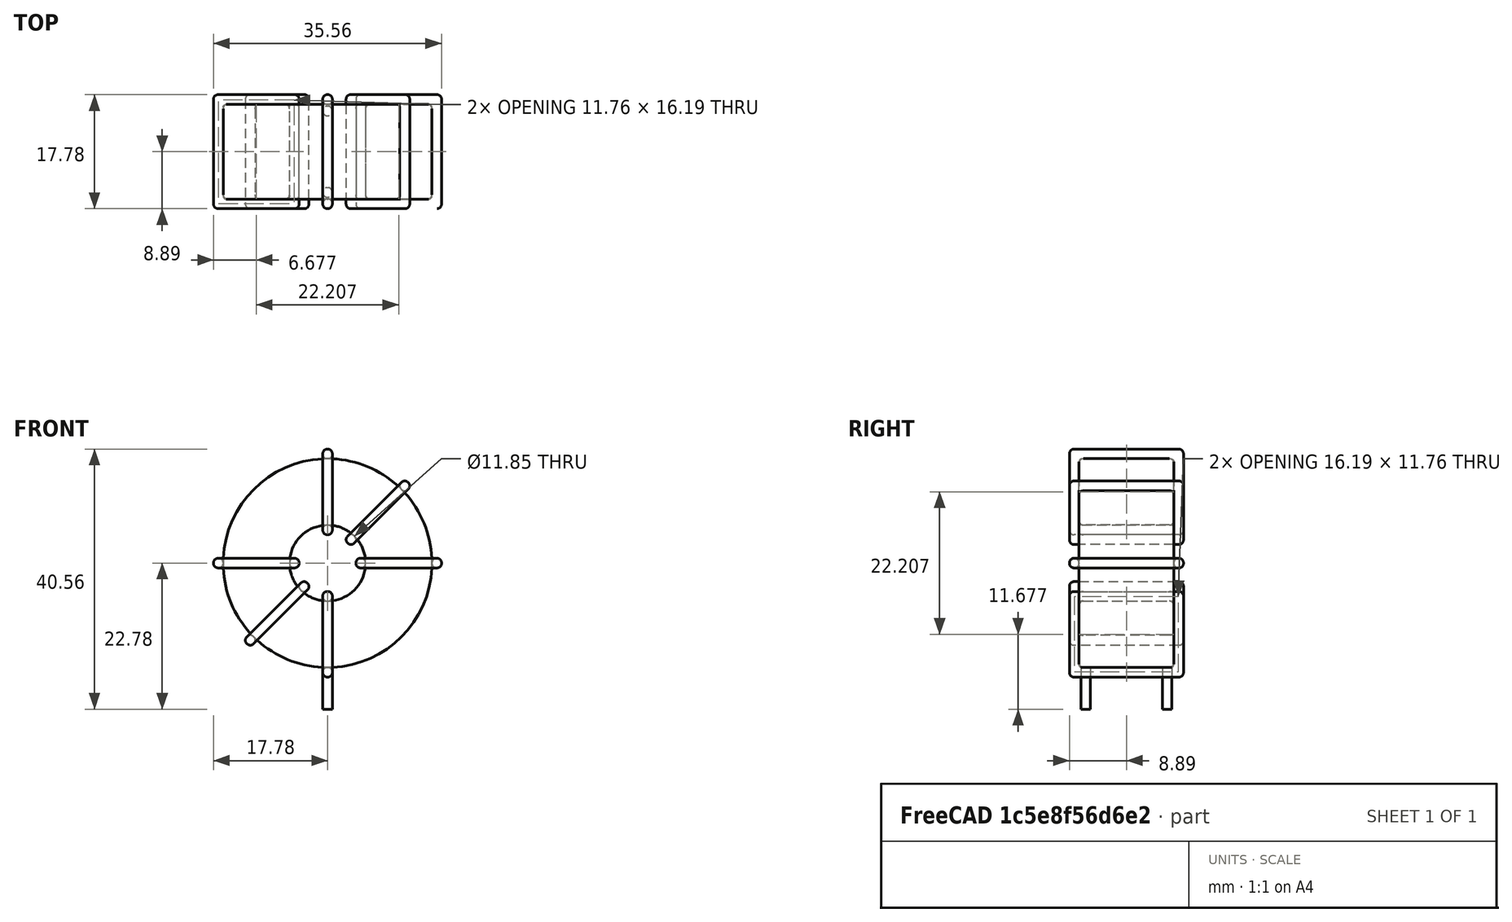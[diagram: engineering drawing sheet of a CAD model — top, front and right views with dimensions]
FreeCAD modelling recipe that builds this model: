
FCSTD DOCUMENT  (FreeCAD 0.16R6703 (Git))
Label: L_Toroid_Vertical_L35.6mm_W17.8mm_P12.70mm_Pulse_E
License: All rights reserved
LicenseURL: http://en.wikipedia.org/wiki/All_rights_reserved
objects: Sketcher::SketchObject×6, PartDesign::Pad×6, PartDesign::Fillet×5, Spreadsheet::Sheet×1
note: 23 computed .brp shape members not serialized (recipe doc carries the construction recipe); baked Part::Feature solids carry a one-line shape summary decoded from their .brp

FEATURE [Spreadsheet::Sheet] Spreadsheet  label="dimensions"
  cells = A1=Wx; B1(Wx)=35.56; C1(WW)=11.85333333333333; D1=35.56; A2=Wy; B2(Wy)=17.78; D2=17.78; A3=RM; B3(RMx)=12.7; C3(RMy)=0; A4=d_wire; B4(d_wire)=1.5; A5=H; B5(H)=35.56; A6=offsetx; B6(offsetx)=17.78
FEATURE [Sketcher::SketchObject] Sketch
  Placement = pos=(0,-6.35,0) rot=(1,0,0;1.5708rad)
  expr: Placement.Base.y = -Spreadsheet.RMx / 2
  expr: Constraints[0] = Spreadsheet.Wx / 2 - Spreadsheet.d_wire
  expr: Constraints[4] = Spreadsheet.WW / 2
  expr: Constraints[2] = Spreadsheet.Wx / 2 + Spreadsheet.d_wire + 0.5
  sketch-geometry (2):
    g0: Circle CenterX=0 CenterY=19.78 CenterZ=0 NormalX=0 NormalY=0 NormalZ=1 Radius=16.28
    g1: Circle CenterX=0 CenterY=19.78 CenterZ=0 NormalX=0 NormalY=0 NormalZ=1 Radius=5.92667
  constraints (5):
    c: Radius(g0) = 16.28
    c: DistanceX(g-1,g0) = 0
    c: DistanceY(g-1,g0) = 19.78
    c: Coincident(g1,g0)
    c: Radius(g1) = 5.92667
FEATURE [PartDesign::Pad] Pad
  Length = 14.78
  Length2 = 100
  Midplane = true
  Placement = pos=(0,-6.35,0) rot=(1,0,0;1.5708rad)
  Sketch = -> Sketch
  Type = 0
  expr: Length = Spreadsheet.Wy - 2 * Spreadsheet.d_wire
FEATURE [Sketcher::SketchObject] Sketch001
  Placement = pos=(0,0,2) rot=(0,0,1;0rad)
  expr: Placement.Base.z = 0.5 + Spreadsheet.d_wire
  expr: Constraints[4] = Spreadsheet.RMy
  expr: Constraints[2] = -Spreadsheet.RMx
  expr: Constraints[1] = Spreadsheet.d_wire / 2
  sketch-geometry (2):
    g0: Circle CenterX=0 CenterY=0 CenterZ=0 NormalX=0 NormalY=0 NormalZ=1 Radius=0.75
    g1: Circle CenterX=0 CenterY=-12.7 CenterZ=0 NormalX=0 NormalY=0 NormalZ=1 Radius=0.75
  constraints (5):
    c: Equal(g0,g1)
    c: Radius(g0) = 0.75
    c: DistanceY(g-1,g1) = -12.7
    c: Coincident(g0,g-1)
    c: DistanceX(g-1,g1) = 0
FEATURE [PartDesign::Pad] Pad001
  Length = 1.5
  Length2 = 5
  Placement = pos=(0,0,2) rot=(0,0,1;0rad)
  Reversed = true
  Sketch = -> Sketch001
  Type = 4
  expr: Length2 = 3.5 + Spreadsheet.d_wire
  expr: Length = Spreadsheet.d_wire
FEATURE [PartDesign::Fillet] Fillet
  Base = -> Pad [Edge6,Edge3,Edge2]
  Placement = pos=(0,-6.35,0) rot=(1,0,0;1.5708rad)
  Radius = 0.5
FEATURE [Sketcher::SketchObject] Sketch003
  Placement = pos=(0,2.54,19.78) rot=(1,0,0;3.14159rad)
  expr: Constraints[18] = Spreadsheet.d_wire
  expr: Constraints[16] = Spreadsheet.d_wire
  expr: Constraints[19] = Spreadsheet.d_wire
  expr: Constraints[17] = Spreadsheet.d_wire
  expr: Placement.Base.y = -1 * (Spreadsheet.RMx - Spreadsheet.Wy) / 2
  expr: Constraints[21] = (Spreadsheet.Wx - Spreadsheet.WW) / 2 - Spreadsheet.d_wire
  expr: Constraints[22] = Spreadsheet.Wx / 2 - Spreadsheet.d_wire
  expr: Constraints[43] = Spreadsheet.d_wire
  expr: Constraints[48] = Spreadsheet.Wx - Spreadsheet.d_wire * 2
  expr: Constraints[49] = Spreadsheet.Wy
  expr: Placement.Base.z = Spreadsheet.Wx / 2 + Spreadsheet.d_wire + 0.5
  sketch-geometry (16):
    g0: LineSegment StartX=-4.42667 StartY=0 StartZ=0 EndX=-17.78 EndY=0 EndZ=0
    g1: LineSegment StartX=-17.78 StartY=0 StartZ=0 EndX=-17.78 EndY=17.78 EndZ=0
    g2: LineSegment StartX=-17.78 StartY=17.78 StartZ=0 EndX=-4.42667 EndY=17.78 EndZ=0
    g3: LineSegment StartX=-4.42667 StartY=17.78 StartZ=0 EndX=-4.42667 EndY=0 EndZ=0
    g4: LineSegment StartX=-16.28 StartY=16.28 StartZ=0 EndX=-5.92667 EndY=16.28 EndZ=0
    g5: LineSegment StartX=-5.92667 StartY=16.28 StartZ=0 EndX=-5.92667 EndY=1.5 EndZ=0
    g6: LineSegment StartX=-5.92667 StartY=1.5 StartZ=0 EndX=-16.28 EndY=1.5 EndZ=0
    g7: LineSegment StartX=-16.28 StartY=1.5 StartZ=0 EndX=-16.28 EndY=16.28 EndZ=0
    g8: LineSegment StartX=4.42667 StartY=17.78 StartZ=0 EndX=17.78 EndY=17.78 EndZ=0
    g9: LineSegment StartX=17.78 StartY=17.78 StartZ=0 EndX=17.78 EndY=0 EndZ=0
    g10: LineSegment StartX=17.78 StartY=0 StartZ=0 EndX=4.42667 EndY=0 EndZ=0
    g11: LineSegment StartX=4.42667 StartY=0 StartZ=0 EndX=4.42667 EndY=17.78 EndZ=0
    g12: LineSegment StartX=5.92667 StartY=16.28 StartZ=0 EndX=16.28 EndY=16.28 EndZ=0
    g13: LineSegment StartX=16.28 StartY=16.28 StartZ=0 EndX=16.28 EndY=1.5 EndZ=0
    g14: LineSegment StartX=16.28 StartY=1.5 StartZ=0 EndX=5.92667 EndY=1.5 EndZ=0
    g15: LineSegment StartX=5.92667 StartY=1.5 StartZ=0 EndX=5.92667 EndY=16.28 EndZ=0
  constraints (50):
    c: Horizontal(g0)
    c: Coincident(g1,g0)
    c: Vertical(g1)
    c: Coincident(g2,g1)
    c: Horizontal(g2)
    c: Coincident(g3,g2)
    c: Coincident(g3,g0)
    c: Vertical(g3)
    c: Coincident(g4,g5)
    c: Coincident(g5,g6)
    c: Coincident(g6,g7)
    c: Coincident(g7,g4)
    c: Horizontal(g4)
    c: Horizontal(g6)
    c: Vertical(g5)
    c: Vertical(g7)
    c: DistanceX(g1,g4) = 1.5
    c: DistanceY(g4,g1) = 1.5
    c: DistanceX(g5,g0) = 1.5
    c: DistanceY(g0,g5) = 1.5
    c: DistanceY(g-1,g0) = 0
    c: DistanceX(g6,g6) = 10.3533
    c: DistanceX(g6,g-1) = 16.28
    c: Coincident(g8,g9)
    c: Coincident(g9,g10)
    c: Coincident(g10,g11)
    c: Coincident(g11,g8)
    c: Horizontal(g8)
    c: Horizontal(g10)
    c: Vertical(g9)
    c: Vertical(g11)
    c: Coincident(g12,g13)
    c: Coincident(g13,g14)
    c: Coincident(g14,g15)
    c: Coincident(g15,g12)
    c: Horizontal(g12)
    c: Horizontal(g14)
    c: Vertical(g13)
    c: Vertical(g15)
    c: DistanceY(g8,g2) = 0
    c: DistanceY(g10,g0) = 0
    c: DistanceY(g14,g5) = 0
    c: DistanceY(g12,g4) = 0
    c: DistanceX(g8,g12) = 1.5
    c: Equal(g8,g2)
    c: Equal(g12,g4)
    c: Equal(g9,g1)
    c: Equal(g13,g7)
    c: DistanceX(g4,g12) = 32.56
    c: DistanceY(g0,g1) = 17.78
FEATURE [PartDesign::Pad] Pad002
  Length = 1.5
  Length2 = 100
  Midplane = true
  Placement = pos=(0,2.54,19.78) rot=(1,0,0;3.14159rad)
  Sketch = -> Sketch003
  Type = 0
  expr: Length = Spreadsheet.d_wire
FEATURE [PartDesign::Fillet] Fillet001
  Base = -> Pad002 [Edge38,Edge41,Edge42,Edge43,Edge29,Edge32,Edge33,Edge34,Edge25,Edge35,Edge36,Edge13,Edge14,Edge15,Edge16,Edge17,Edge18,Edge19,Edge1,Edge2,Edge3,Edge4,Edge5,Edge6,Edge7,Edge37,Edge39,Edge40,Edge20,Edge23,Edge24,Edge21,Edge22,Edge8,Edge9,Edge10,Edge11,Edge12,Edge26,Edge27,+8 more]
  Placement = pos=(0,2.54,19.78) rot=(1,0,0;3.14159rad)
  Radius = 0.705
  expr: Radius = Spreadsheet.d_wire * 0.47
FEATURE [Sketcher::SketchObject] Sketch004
  Placement = pos=(0,2.54,19.78) rot=(0.92388,0,0.382683;3.14159rad)
  expr: Constraints[18] = Spreadsheet.d_wire
  expr: Constraints[16] = Spreadsheet.d_wire
  expr: Constraints[19] = Spreadsheet.d_wire
  expr: Constraints[17] = Spreadsheet.d_wire
  expr: Placement.Base.y = -1 * (Spreadsheet.RMx - Spreadsheet.Wy) / 2
  expr: Constraints[21] = (Spreadsheet.Wx - Spreadsheet.WW) / 2 - Spreadsheet.d_wire
  expr: Constraints[22] = Spreadsheet.Wx / 2 - Spreadsheet.d_wire
  expr: Constraints[43] = Spreadsheet.d_wire
  expr: Constraints[48] = Spreadsheet.Wx - 2 * Spreadsheet.d_wire
  expr: Constraints[49] = Spreadsheet.Wy
  expr: Placement.Base.z = Spreadsheet.Wx / 2 + Spreadsheet.d_wire + 0.5
  sketch-geometry (16):
    g0: LineSegment StartX=-4.42667 StartY=0 StartZ=0 EndX=-17.78 EndY=0 EndZ=0
    g1: LineSegment StartX=-17.78 StartY=0 StartZ=0 EndX=-17.78 EndY=17.78 EndZ=0
    g2: LineSegment StartX=-17.78 StartY=17.78 StartZ=0 EndX=-4.42667 EndY=17.78 EndZ=0
    g3: LineSegment StartX=-4.42667 StartY=17.78 StartZ=0 EndX=-4.42667 EndY=0 EndZ=0
    g4: LineSegment StartX=-16.28 StartY=16.28 StartZ=0 EndX=-5.92667 EndY=16.28 EndZ=0
    g5: LineSegment StartX=-5.92667 StartY=16.28 StartZ=0 EndX=-5.92667 EndY=1.5 EndZ=0
    g6: LineSegment StartX=-5.92667 StartY=1.5 StartZ=0 EndX=-16.28 EndY=1.5 EndZ=0
    g7: LineSegment StartX=-16.28 StartY=1.5 StartZ=0 EndX=-16.28 EndY=16.28 EndZ=0
    g8: LineSegment StartX=4.42667 StartY=17.78 StartZ=0 EndX=17.78 EndY=17.78 EndZ=0
    g9: LineSegment StartX=17.78 StartY=17.78 StartZ=0 EndX=17.78 EndY=0 EndZ=0
    g10: LineSegment StartX=17.78 StartY=0 StartZ=0 EndX=4.42667 EndY=0 EndZ=0
    g11: LineSegment StartX=4.42667 StartY=0 StartZ=0 EndX=4.42667 EndY=17.78 EndZ=0
    g12: LineSegment StartX=5.92667 StartY=16.28 StartZ=0 EndX=16.28 EndY=16.28 EndZ=0
    g13: LineSegment StartX=16.28 StartY=16.28 StartZ=0 EndX=16.28 EndY=1.5 EndZ=0
    g14: LineSegment StartX=16.28 StartY=1.5 StartZ=0 EndX=5.92667 EndY=1.5 EndZ=0
    g15: LineSegment StartX=5.92667 StartY=1.5 StartZ=0 EndX=5.92667 EndY=16.28 EndZ=0
  constraints (50):
    c: Horizontal(g0)
    c: Coincident(g1,g0)
    c: Vertical(g1)
    c: Coincident(g2,g1)
    c: Horizontal(g2)
    c: Coincident(g3,g2)
    c: Coincident(g3,g0)
    c: Vertical(g3)
    c: Coincident(g4,g5)
    c: Coincident(g5,g6)
    c: Coincident(g6,g7)
    c: Coincident(g7,g4)
    c: Horizontal(g4)
    c: Horizontal(g6)
    c: Vertical(g5)
    c: Vertical(g7)
    c: DistanceX(g1,g4) = 1.5
    c: DistanceY(g4,g1) = 1.5
    c: DistanceX(g5,g0) = 1.5
    c: DistanceY(g0,g5) = 1.5
    c: DistanceY(g-1,g0) = 0
    c: DistanceX(g6,g6) = 10.3533
    c: DistanceX(g6,g-1) = 16.28
    c: Coincident(g8,g9)
    c: Coincident(g9,g10)
    c: Coincident(g10,g11)
    c: Coincident(g11,g8)
    c: Horizontal(g8)
    c: Horizontal(g10)
    c: Vertical(g9)
    c: Vertical(g11)
    c: Coincident(g12,g13)
    c: Coincident(g13,g14)
    c: Coincident(g14,g15)
    c: Coincident(g15,g12)
    c: Horizontal(g12)
    c: Horizontal(g14)
    c: Vertical(g13)
    c: Vertical(g15)
    c: DistanceY(g8,g2) = 0
    c: DistanceY(g10,g0) = 0
    c: DistanceY(g14,g5) = 0
    c: DistanceY(g12,g4) = 0
    c: DistanceX(g8,g12) = 1.5
    c: Equal(g8,g2)
    c: Equal(g12,g4)
    c: Equal(g9,g1)
    c: Equal(g13,g7)
    c: DistanceX(g4,g12) = 32.56
    c: DistanceY(g0,g1) = 17.78
FEATURE [PartDesign::Pad] Pad003
  Length = 1.5
  Length2 = 100
  Midplane = true
  Placement = pos=(0,2.54,19.78) rot=(0.92388,0,0.382683;3.14159rad)
  Sketch = -> Sketch004
  Type = 0
  expr: Length = Spreadsheet.d_wire
FEATURE [PartDesign::Fillet] Fillet002
  Base = -> Pad003 [Edge38,Edge41,Edge42,Edge43,Edge29,Edge32,Edge33,Edge34,Edge25,Edge35,Edge36,Edge13,Edge14,Edge15,Edge16,Edge17,Edge18,Edge19,Edge1,Edge2,Edge3,Edge4,Edge5,Edge6,Edge7,Edge37,Edge39,Edge40,Edge20,Edge23,Edge24,Edge21,Edge22,Edge8,Edge9,Edge10,Edge11,Edge12,Edge26,Edge27,+8 more]
  Placement = pos=(0,2.54,19.78) rot=(0.92388,0,0.382683;3.14159rad)
  Radius = 0.705
  expr: Radius = Spreadsheet.d_wire * 0.47
FEATURE [Sketcher::SketchObject] Sketch005
  Placement = pos=(0,2.54,19.78) rot=(0.92388,0,-0.382683;3.14159rad)
  expr: Constraints[18] = Spreadsheet.d_wire
  expr: Constraints[16] = Spreadsheet.d_wire
  expr: Constraints[19] = Spreadsheet.d_wire
  expr: Constraints[17] = Spreadsheet.d_wire
  expr: Placement.Base.y = -1 * (Spreadsheet.RMx - Spreadsheet.Wy) / 2
  expr: Constraints[21] = (Spreadsheet.Wx - Spreadsheet.WW) / 2 - Spreadsheet.d_wire
  expr: Constraints[22] = Spreadsheet.Wx / 2 - Spreadsheet.d_wire
  expr: Constraints[43] = Spreadsheet.d_wire
  expr: Constraints[48] = Spreadsheet.Wx - 2 * Spreadsheet.d_wire
  expr: Constraints[49] = Spreadsheet.Wy
  expr: Placement.Base.z = Spreadsheet.Wx / 2 + Spreadsheet.d_wire + 0.5
  sketch-geometry (16):
    g0: LineSegment StartX=-4.42667 StartY=0 StartZ=0 EndX=-17.78 EndY=0 EndZ=0
    g1: LineSegment StartX=-17.78 StartY=0 StartZ=0 EndX=-17.78 EndY=17.78 EndZ=0
    g2: LineSegment StartX=-17.78 StartY=17.78 StartZ=0 EndX=-4.42667 EndY=17.78 EndZ=0
    g3: LineSegment StartX=-4.42667 StartY=17.78 StartZ=0 EndX=-4.42667 EndY=0 EndZ=0
    g4: LineSegment StartX=-16.28 StartY=16.28 StartZ=0 EndX=-5.92667 EndY=16.28 EndZ=0
    g5: LineSegment StartX=-5.92667 StartY=16.28 StartZ=0 EndX=-5.92667 EndY=1.5 EndZ=0
    g6: LineSegment StartX=-5.92667 StartY=1.5 StartZ=0 EndX=-16.28 EndY=1.5 EndZ=0
    g7: LineSegment StartX=-16.28 StartY=1.5 StartZ=0 EndX=-16.28 EndY=16.28 EndZ=0
    g8: LineSegment StartX=4.42667 StartY=17.78 StartZ=0 EndX=17.78 EndY=17.78 EndZ=0
    g9: LineSegment StartX=17.78 StartY=17.78 StartZ=0 EndX=17.78 EndY=0 EndZ=0
    g10: LineSegment StartX=17.78 StartY=0 StartZ=0 EndX=4.42667 EndY=0 EndZ=0
    g11: LineSegment StartX=4.42667 StartY=0 StartZ=0 EndX=4.42667 EndY=17.78 EndZ=0
    g12: LineSegment StartX=5.92667 StartY=16.28 StartZ=0 EndX=16.28 EndY=16.28 EndZ=0
    g13: LineSegment StartX=16.28 StartY=16.28 StartZ=0 EndX=16.28 EndY=1.5 EndZ=0
    g14: LineSegment StartX=16.28 StartY=1.5 StartZ=0 EndX=5.92667 EndY=1.5 EndZ=0
    g15: LineSegment StartX=5.92667 StartY=1.5 StartZ=0 EndX=5.92667 EndY=16.28 EndZ=0
  constraints (50):
    c: Horizontal(g0)
    c: Coincident(g1,g0)
    c: Vertical(g1)
    c: Coincident(g2,g1)
    c: Horizontal(g2)
    c: Coincident(g3,g2)
    c: Coincident(g3,g0)
    c: Vertical(g3)
    c: Coincident(g4,g5)
    c: Coincident(g5,g6)
    c: Coincident(g6,g7)
    c: Coincident(g7,g4)
    c: Horizontal(g4)
    c: Horizontal(g6)
    c: Vertical(g5)
    c: Vertical(g7)
    c: DistanceX(g1,g4) = 1.5
    c: DistanceY(g4,g1) = 1.5
    c: DistanceX(g5,g0) = 1.5
    c: DistanceY(g0,g5) = 1.5
    c: DistanceY(g-1,g0) = 0
    c: DistanceX(g6,g6) = 10.3533
    c: DistanceX(g6,g-1) = 16.28
    c: Coincident(g8,g9)
    c: Coincident(g9,g10)
    c: Coincident(g10,g11)
    c: Coincident(g11,g8)
    c: Horizontal(g8)
    c: Horizontal(g10)
    c: Vertical(g9)
    c: Vertical(g11)
    c: Coincident(g12,g13)
    c: Coincident(g13,g14)
    c: Coincident(g14,g15)
    c: Coincident(g15,g12)
    c: Horizontal(g12)
    c: Horizontal(g14)
    c: Vertical(g13)
    c: Vertical(g15)
    c: DistanceY(g8,g2) = 0
    c: DistanceY(g10,g0) = 0
    c: DistanceY(g14,g5) = 0
    c: DistanceY(g12,g4) = 0
    c: DistanceX(g8,g12) = 1.5
    c: Equal(g8,g2)
    c: Equal(g12,g4)
    c: Equal(g9,g1)
    c: Equal(g13,g7)
    c: DistanceX(g4,g12) = 32.56
    c: DistanceY(g0,g1) = 17.78
FEATURE [PartDesign::Pad] Pad004
  Length = 1.5
  Length2 = 100
  Midplane = true
  Placement = pos=(0,2.54,19.78) rot=(0.92388,0,-0.382683;3.14159rad)
  Sketch = -> Sketch005
  Type = 0
  expr: Length = Spreadsheet.d_wire
FEATURE [PartDesign::Fillet] Fillet003
  Base = -> Pad004 [Edge38,Edge41,Edge42,Edge43,Edge29,Edge32,Edge33,Edge34,Edge25,Edge35,Edge36,Edge13,Edge14,Edge15,Edge16,Edge17,Edge18,Edge19,Edge1,Edge2,Edge3,Edge4,Edge5,Edge6,Edge7,Edge37,Edge39,Edge40,Edge20,Edge23,Edge24,Edge21,Edge22,Edge8,Edge9,Edge10,Edge11,Edge12,Edge26,Edge27,+8 more]
  Placement = pos=(0,2.54,19.78) rot=(0.92388,0,-0.382683;3.14159rad)
  Radius = 0.705
  expr: Radius = Spreadsheet.d_wire * 0.47
FEATURE [Sketcher::SketchObject] Sketch006
  Placement = pos=(0,2.54,19.78) rot=(0.707107,0,0.707107;3.14159rad)
  expr: Constraints[18] = Spreadsheet.d_wire
  expr: Constraints[16] = Spreadsheet.d_wire
  expr: Constraints[19] = Spreadsheet.d_wire
  expr: Constraints[17] = Spreadsheet.d_wire
  expr: Placement.Base.y = -1 * (Spreadsheet.RMx - Spreadsheet.Wy) / 2
  expr: Constraints[21] = (Spreadsheet.Wx - Spreadsheet.WW) / 2 - Spreadsheet.d_wire
  expr: Constraints[22] = Spreadsheet.Wx / 2 - Spreadsheet.d_wire
  expr: Constraints[43] = Spreadsheet.d_wire
  expr: Constraints[48] = Spreadsheet.Wx - Spreadsheet.d_wire * 2
  expr: Constraints[49] = Spreadsheet.Wy
  expr: Placement.Base.z = Spreadsheet.Wx / 2 + Spreadsheet.d_wire + 0.5
  sketch-geometry (16):
    g0: LineSegment StartX=-4.42667 StartY=0 StartZ=0 EndX=-17.78 EndY=0 EndZ=0
    g1: LineSegment StartX=-17.78 StartY=0 StartZ=0 EndX=-17.78 EndY=17.78 EndZ=0
    g2: LineSegment StartX=-17.78 StartY=17.78 StartZ=0 EndX=-4.42667 EndY=17.78 EndZ=0
    g3: LineSegment StartX=-4.42667 StartY=17.78 StartZ=0 EndX=-4.42667 EndY=0 EndZ=0
    g4: LineSegment StartX=-16.28 StartY=16.28 StartZ=0 EndX=-5.92667 EndY=16.28 EndZ=0
    g5: LineSegment StartX=-5.92667 StartY=16.28 StartZ=0 EndX=-5.92667 EndY=1.5 EndZ=0
    g6: LineSegment StartX=-5.92667 StartY=1.5 StartZ=0 EndX=-16.28 EndY=1.5 EndZ=0
    g7: LineSegment StartX=-16.28 StartY=1.5 StartZ=0 EndX=-16.28 EndY=16.28 EndZ=0
    g8: LineSegment StartX=4.42667 StartY=17.78 StartZ=0 EndX=17.78 EndY=17.78 EndZ=0
    g9: LineSegment StartX=17.78 StartY=17.78 StartZ=0 EndX=17.78 EndY=0 EndZ=0
    g10: LineSegment StartX=17.78 StartY=0 StartZ=0 EndX=4.42667 EndY=0 EndZ=0
    g11: LineSegment StartX=4.42667 StartY=0 StartZ=0 EndX=4.42667 EndY=17.78 EndZ=0
    g12: LineSegment StartX=5.92667 StartY=16.28 StartZ=0 EndX=16.28 EndY=16.28 EndZ=0
    g13: LineSegment StartX=16.28 StartY=16.28 StartZ=0 EndX=16.28 EndY=1.5 EndZ=0
    g14: LineSegment StartX=16.28 StartY=1.5 StartZ=0 EndX=5.92667 EndY=1.5 EndZ=0
    g15: LineSegment StartX=5.92667 StartY=1.5 StartZ=0 EndX=5.92667 EndY=16.28 EndZ=0
  constraints (50):
    c: Horizontal(g0)
    c: Coincident(g1,g0)
    c: Vertical(g1)
    c: Coincident(g2,g1)
    c: Horizontal(g2)
    c: Coincident(g3,g2)
    c: Coincident(g3,g0)
    c: Vertical(g3)
    c: Coincident(g4,g5)
    c: Coincident(g5,g6)
    c: Coincident(g6,g7)
    c: Coincident(g7,g4)
    c: Horizontal(g4)
    c: Horizontal(g6)
    c: Vertical(g5)
    c: Vertical(g7)
    c: DistanceX(g1,g4) = 1.5
    c: DistanceY(g4,g1) = 1.5
    c: DistanceX(g5,g0) = 1.5
    c: DistanceY(g0,g5) = 1.5
    c: DistanceY(g-1,g0) = 0
    c: DistanceX(g6,g6) = 10.3533
    c: DistanceX(g6,g-1) = 16.28
    c: Coincident(g8,g9)
    c: Coincident(g9,g10)
    c: Coincident(g10,g11)
    c: Coincident(g11,g8)
    c: Horizontal(g8)
    c: Horizontal(g10)
    c: Vertical(g9)
    c: Vertical(g11)
    c: Coincident(g12,g13)
    c: Coincident(g13,g14)
    c: Coincident(g14,g15)
    c: Coincident(g15,g12)
    c: Horizontal(g12)
    c: Horizontal(g14)
    c: Vertical(g13)
    c: Vertical(g15)
    c: DistanceY(g8,g2) = 0
    c: DistanceY(g10,g0) = 0
    c: DistanceY(g14,g5) = 0
    c: DistanceY(g12,g4) = 0
    c: DistanceX(g8,g12) = 1.5
    c: Equal(g8,g2)
    c: Equal(g12,g4)
    c: Equal(g9,g1)
    c: Equal(g13,g7)
    c: DistanceX(g4,g12) = 32.56
    c: DistanceY(g0,g1) = 17.78
FEATURE [PartDesign::Pad] Pad005
  Length = 1.5
  Length2 = 100
  Midplane = true
  Placement = pos=(0,2.54,19.78) rot=(0.707107,0,0.707107;3.14159rad)
  Sketch = -> Sketch006
  Type = 0
  expr: Length = Spreadsheet.d_wire
FEATURE [PartDesign::Fillet] Fillet004
  Base = -> Pad005 [Edge38,Edge41,Edge42,Edge43,Edge29,Edge32,Edge33,Edge34,Edge25,Edge35,Edge36,Edge13,Edge14,Edge15,Edge16,Edge17,Edge18,Edge19,Edge1,Edge2,Edge3,Edge4,Edge5,Edge6,Edge7,Edge37,Edge39,Edge40,Edge20,Edge23,Edge24,Edge21,Edge22,Edge8,Edge9,Edge10,Edge11,Edge12,Edge26,Edge27,+8 more]
  Placement = pos=(0,2.54,19.78) rot=(0.707107,0,0.707107;3.14159rad)
  Radius = 0.705
  expr: Radius = Spreadsheet.d_wire * 0.47
